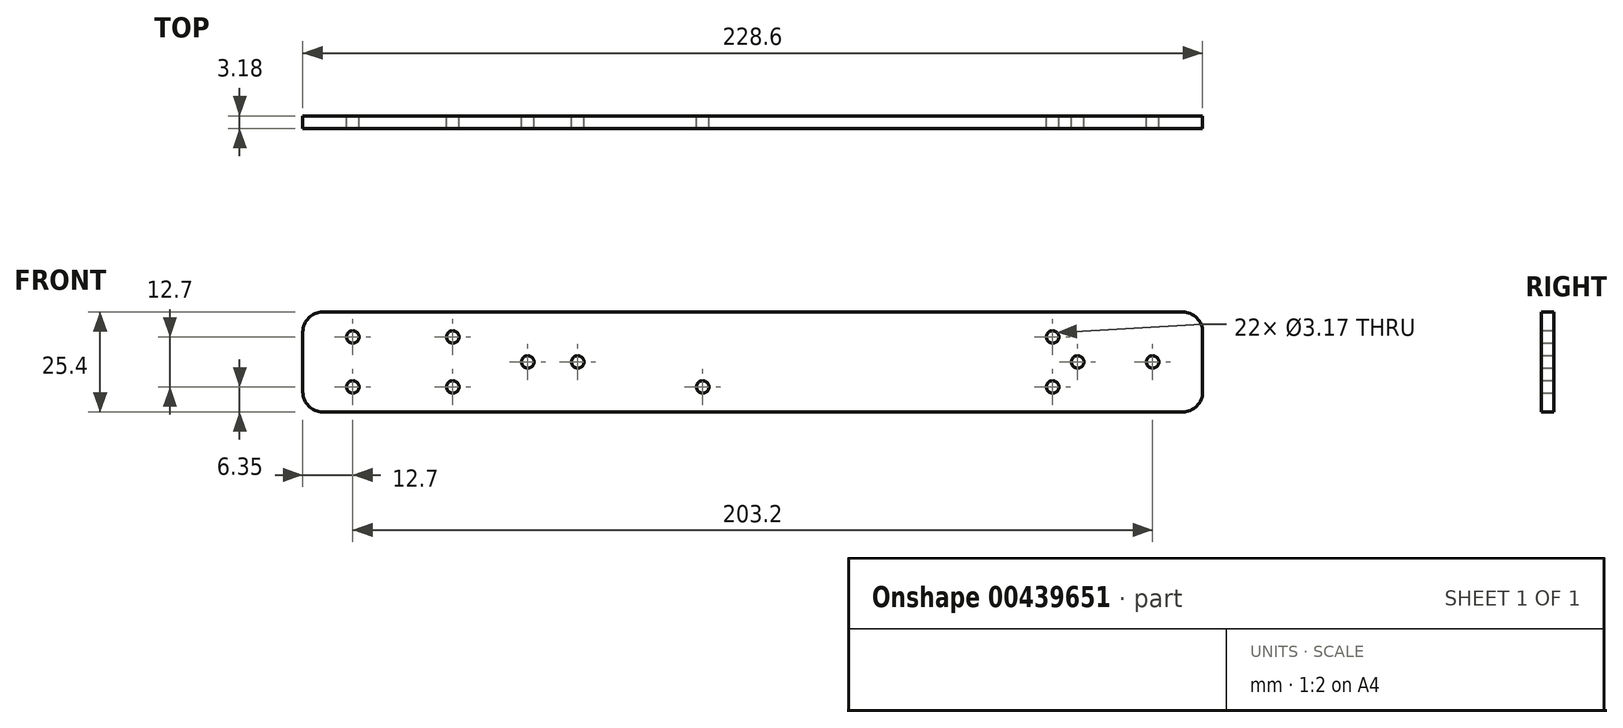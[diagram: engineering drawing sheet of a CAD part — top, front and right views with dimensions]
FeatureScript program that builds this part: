
annotation { "Feature Type Name" : "Feature", "Feature Type Description" : "" }
export const myFeature = defineFeature(function(context is Context, id is Id, definition is map)
    precondition{}
    {
        {
            var Q0;
            Q0=qCreatedBy(makeId("Front.planeOp"),FACE);
            var sketch = newSketch(context, id + "F0", { "sketchPlane" : qUnion([Q0])});
            skLineSegment(sketch, "E0.bottom", {"start": v(-102.5, 19.05) * mm, "end": v(126.1, 19.05) * mm});
            skLineSegment(sketch, "E0.top", {"start": v(-102.5, -6.35) * mm, "end": v(126.1, -6.35) * mm});
            skLineSegment(sketch, "E0.left", {"start": v(-102.5, 19.05) * mm, "end": v(-102.5, -6.35) * mm});
            skLineSegment(sketch, "E0.right", {"start": v(126.1, 19.05) * mm, "end": v(126.1, -6.35) * mm});
            skPoint(sketch, "E1", {"position": v(-89.8, 12.7) * mm});
            skPoint(sketch, "E2", {"position": v(-45.35, 6.35) * mm});
            skPoint(sketch, "E3", {"position": v(-32.65, 6.35) * mm});
            skPoint(sketch, "E4", {"position": v(-0.9, 0) * mm});
            skPoint(sketch, "E5", {"position": v(47.49, 46.91) * mm});
            skPoint(sketch, "E6", {"position": v(90.66, 46.91) * mm});
            skPoint(sketch, "E7", {"position": v(88, 12.7) * mm});
            skPoint(sketch, "E8", {"position": v(88, 0) * mm});
            skPoint(sketch, "E9", {"position": v(113.4, 6.35) * mm});
            skPoint(sketch, "E10", {"position": v(94.35, 6.35) * mm});
            skCircle(sketch, "E11", {"center": v(-89.8, 12.7) * mm, "radius": 1.59 * mm});
            skCircle(sketch, "E12", {"center": v(-89.8, 0) * mm, "radius": 1.59 * mm});
            skCircle(sketch, "E13", {"center": v(-45.35, 6.35) * mm, "radius": 1.59 * mm});
            skCircle(sketch, "E14", {"center": v(-32.65, 6.35) * mm, "radius": 1.59 * mm});
            skCircle(sketch, "E15", {"center": v(-0.9, 0) * mm, "radius": 1.59 * mm});
            skCircle(sketch, "E16", {"center": v(94.35, 6.35) * mm, "radius": 1.59 * mm});
            skCircle(sketch, "E17", {"center": v(88, 12.7) * mm, "radius": 1.59 * mm});
            skCircle(sketch, "E18", {"center": v(113.4, 6.35) * mm, "radius": 1.59 * mm});
            skCircle(sketch, "E19", {"center": v(88, 0) * mm, "radius": 1.59 * mm});
            skPoint(sketch, "E20", {"position": v(-64.4, 12.7) * mm});
            skPoint(sketch, "E21", {"position": v(-64.4, 0) * mm});
            skCircle(sketch, "E22", {"center": v(-64.4, 12.7) * mm, "radius": 1.59 * mm});
            skCircle(sketch, "E23", {"center": v(-64.4, 0) * mm, "radius": 1.59 * mm});
            skSolve(sketch);
        }
        {
            var Q0;
            Q0=makeQuery(id+"F0.imprint","IMPRINT",FACE,{"disambiguationData":[TD([[makeQuery(id+"F0.imprint","IMPRINT",EDGE,{"derivedFrom":sQuery(id+"F0.wireOp",EDGE,"E0.bottom")}),-1.0]])]});
            extrude(context, id + "F1", {"entities" : qUnion([Q0]), "endBound" : BoundingType.SYMMETRIC, "depth" : 3.17 * mm});
        }
        {
            var Q0;
            Q0=makeQuery(id+"F1.opExtrude","SWEPT_EDGE",EDGE,{"disambiguationData":[OSD([sQuery(id+"F0.wireOp",EDGE,"E0.bottom"),sQuery(id+"F0.wireOp",EDGE,"E0.left")])]});
            var Q1;
            Q1=makeQuery(id+"F1.opExtrude","SWEPT_EDGE",EDGE,{"disambiguationData":[OSD([sQuery(id+"F0.wireOp",EDGE,"E0.top"),sQuery(id+"F0.wireOp",EDGE,"E0.left")])]});
            var Q2;
            Q2=makeQuery(id+"F1.opExtrude","SWEPT_EDGE",EDGE,{"disambiguationData":[OSD([sQuery(id+"F0.wireOp",EDGE,"E0.bottom"),sQuery(id+"F0.wireOp",EDGE,"E0.right")])]});
            var Q3;
            Q3=makeQuery(id+"F1.opExtrude","SWEPT_EDGE",EDGE,{"disambiguationData":[OSD([sQuery(id+"F0.wireOp",EDGE,"E0.top"),sQuery(id+"F0.wireOp",EDGE,"E0.right")])]});
            fillet(context, id + "F2", {"entities" : qUnion([Q0, Q1, Q2, Q3]), "radius" : 5.08 * mm, "tangentPropagation" : true, "allowEdgeOverflow" : false});
        }
    });
